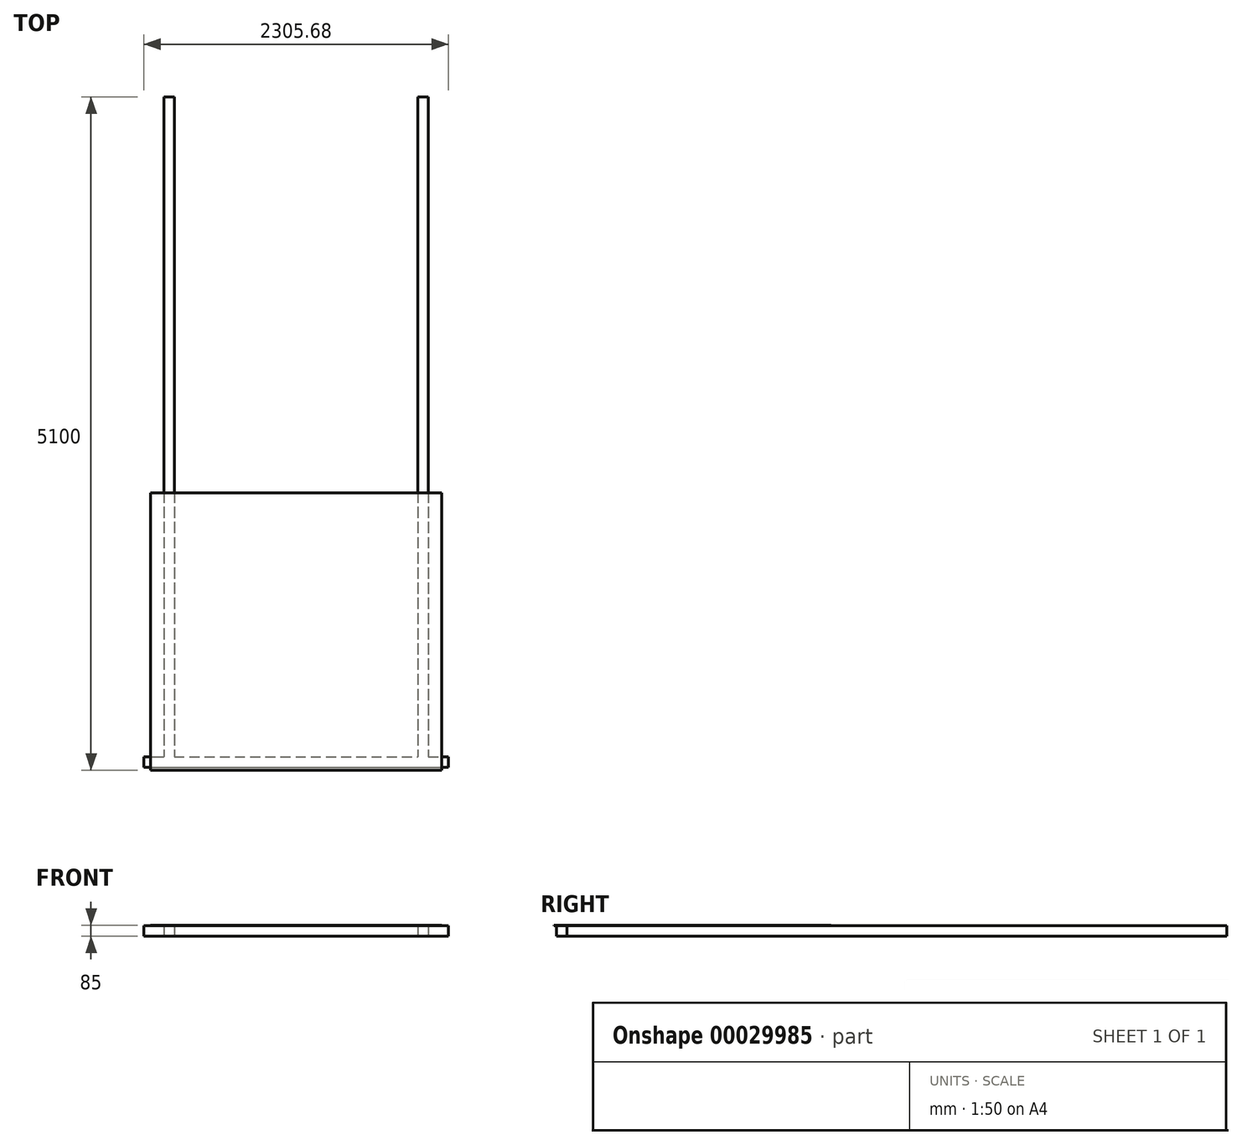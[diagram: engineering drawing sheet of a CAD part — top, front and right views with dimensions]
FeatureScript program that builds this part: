
annotation { "Feature Type Name" : "Feature", "Feature Type Description" : "" }
export const myFeature = defineFeature(function(context is Context, id is Id, definition is map)
    precondition{}
    {
        {
            var Q0;
            Q0=qCreatedBy(makeId("Top.planeOp"),FACE);
            var sketch = newSketch(context, id + "F0", { "sketchPlane" : qUnion([Q0])});
            skLineSegment(sketch, "E0", {"start": v(0, 2767.22) * mm, "end": v(0, 0) * mm, "construction": true});
            skLineSegment(sketch, "E1", {"start": v(0, 0) * mm, "end": v(4273.6, 0) * mm, "construction": true});
            skLineSegment(sketch, "E2.bottom", {"start": v(-1002.85, 2540) * mm, "end": v(-922.84, 2540) * mm});
            skLineSegment(sketch, "E2.top", {"start": v(-1002.84, -2460) * mm, "end": v(-922.84, -2460) * mm});
            skLineSegment(sketch, "E2.left", {"start": v(-1002.85, 2540) * mm, "end": v(-1002.85, -2460) * mm});
            skLineSegment(sketch, "E2.right", {"start": v(-922.84, 2540) * mm, "end": v(-922.85, -2460) * mm});
            skLineSegment(sketch, "E3.bottom", {"start": v(922.84, 2540) * mm, "end": v(1002.84, 2540) * mm});
            skLineSegment(sketch, "E3.top", {"start": v(922.84, -2460) * mm, "end": v(1002.84, -2460) * mm});
            skLineSegment(sketch, "E3.left", {"start": v(922.85, 2540) * mm, "end": v(922.84, -2460) * mm});
            skLineSegment(sketch, "E3.right", {"start": v(1002.85, 2540) * mm, "end": v(1002.85, -2460) * mm});
            skLineSegment(sketch, "E4.bottom", {"start": v(-1152.84, -2460) * mm, "end": v(1152.84, -2460) * mm});
            skLineSegment(sketch, "E4.top", {"start": v(-1152.84, -2540) * mm, "end": v(1152.84, -2540) * mm});
            skLineSegment(sketch, "E4.left", {"start": v(-1152.85, -2460) * mm, "end": v(-1152.85, -2540) * mm});
            skLineSegment(sketch, "E4.right", {"start": v(1152.84, -2460) * mm, "end": v(1152.84, -2540) * mm});
            skSolve(sketch);
        }
        {
            var Q0;
            Q0 = qSketchRegion(id + "F0", true);
            extrude(context, id + "F1", {"entities" : qUnion([Q0]), "depth" : 80 * mm});
        }
        {
            var Q0;
            Q0=makeQuery(id+"F1.opExtrude","CAP_FACE",FACE,{"disambiguationData":[OSD([sQuery(id+"F0.wireOp",EDGE,"E2.bottom"),sQuery(id+"F0.wireOp",EDGE,"E2.left"),sQuery(id+"F0.wireOp",EDGE,"E2.right"),sQuery(id+"F0.wireOp",EDGE,"E3.bottom"),sQuery(id+"F0.wireOp",EDGE,"E3.left"),sQuery(id+"F0.wireOp",EDGE,"E3.right"),sQuery(id+"F0.wireOp",EDGE,"E4.bottom"),sQuery(id+"F0.wireOp",EDGE,"E4.top"),sQuery(id+"F0.wireOp",EDGE,"E4.left"),sQuery(id+"F0.wireOp",EDGE,"E4.right")])],"isStart":false});
            var sketch = newSketch(context, id + "F2", { "sketchPlane" : qUnion([Q0])});
            skLineSegment(sketch, "E5.bottom", {"start": v(-1102.84, -460) * mm, "end": v(1102.84, -460) * mm});
            skLineSegment(sketch, "E5.top", {"start": v(-1102.84, -2560) * mm, "end": v(1102.85, -2560) * mm});
            skLineSegment(sketch, "E5.left", {"start": v(-1102.84, -460) * mm, "end": v(-1102.84, -2560) * mm});
            skLineSegment(sketch, "E5.right", {"start": v(1102.85, -460) * mm, "end": v(1102.85, -2560) * mm});
            skLineSegment(sketch, "E6", {"start": v(0, 0) * mm, "end": v(0, -1948.76) * mm, "construction": true});
            skSolve(sketch);
        }
        {
            var Q0;
            Q0 = qSketchRegion(id + "F2", true);
            extrude(context, id + "F3", {"entities" : qUnion([Q0]), "operationType" : NewBodyOperationType.ADD, "depth" : 5 * mm});
        }
    });
